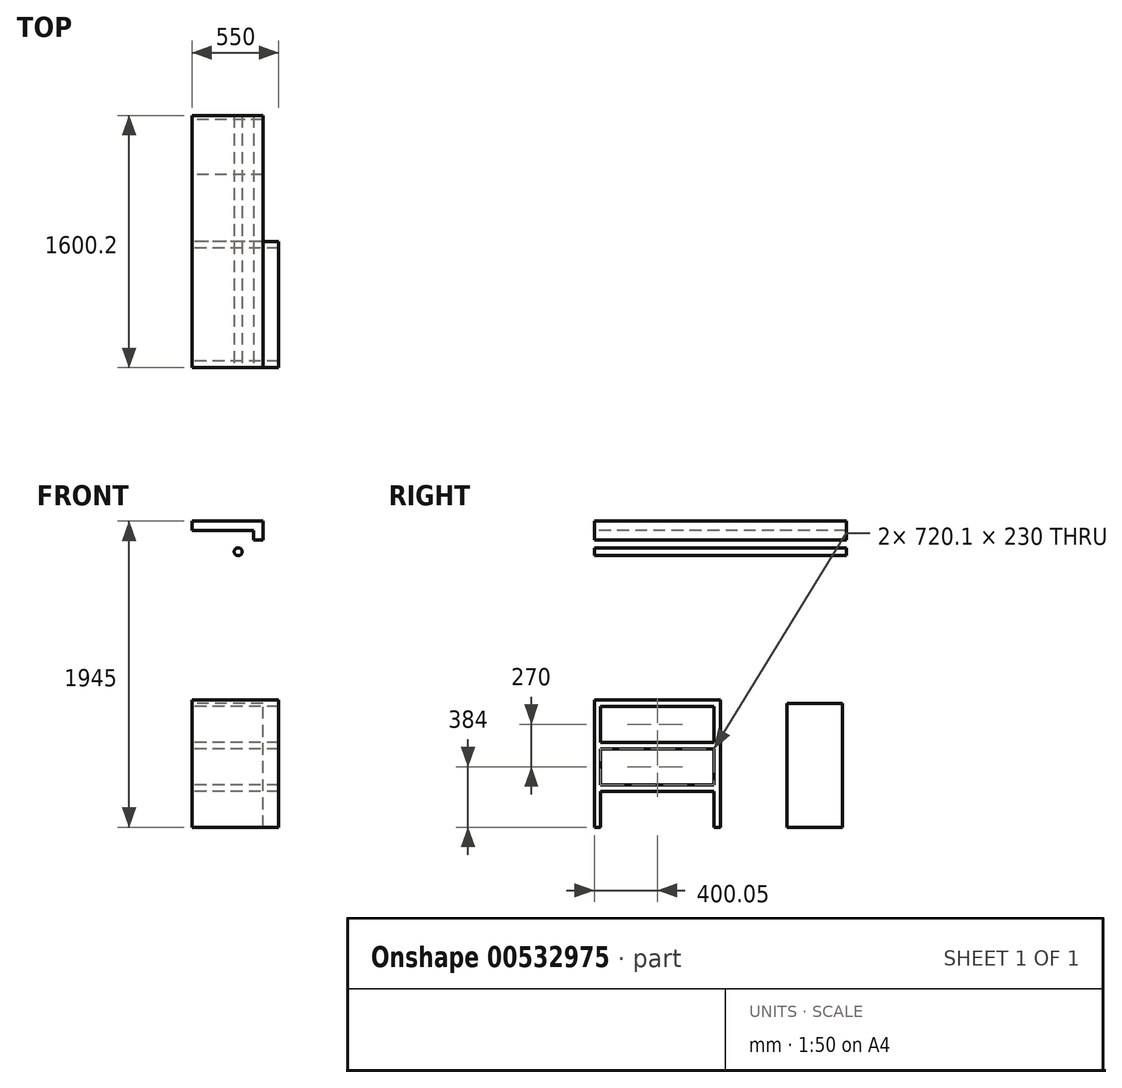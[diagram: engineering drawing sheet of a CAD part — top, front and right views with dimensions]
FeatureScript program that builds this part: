
annotation { "Feature Type Name" : "Feature", "Feature Type Description" : "" }
export const myFeature = defineFeature(function(context is Context, id is Id, definition is map)
    precondition{}
    {
        {
            var Q0;
            Q0=qCreatedBy(makeId("Front.planeOp"),FACE);
            var sketch = newSketch(context, id + "F0", { "sketchPlane" : qUnion([Q0])});
            skLineSegment(sketch, "E0.bottom", {"start": v(0, 0) * mm, "end": v(584.2, 0) * mm});
            skLineSegment(sketch, "E0.top", {"start": v(0, 2311.4) * mm, "end": v(584.2, 2311.4) * mm});
            skLineSegment(sketch, "E0.left", {"start": v(0, 0) * mm, "end": v(0, 2311.4) * mm});
            skLineSegment(sketch, "E0.right", {"start": v(584.2, 0) * mm, "end": v(584.2, 2311.4) * mm});
            skSolve(sketch);
        }
        {
            var Q0;
            Q0=qCreatedBy(makeId("Right.planeOp"),FACE);
            var sketch = newSketch(context, id + "F1", { "sketchPlane" : qUnion([Q0])});
            skLineSegment(sketch, "E1.bottom", {"start": v(0, 0) * mm, "end": v(1600.2, 0) * mm});
            skLineSegment(sketch, "E1.top", {"start": v(0, 2311.4) * mm, "end": v(1600.2, 2311.4) * mm});
            skLineSegment(sketch, "E1.left", {"start": v(0, 0) * mm, "end": v(0, 2311.4) * mm});
            skLineSegment(sketch, "E1.right", {"start": v(1600.2, 0) * mm, "end": v(1600.2, 2311.4) * mm});
            skSolve(sketch);
        }
        {
            var Q0;
            Q0=qCreatedBy(makeId("Front.planeOp"),FACE);
            var Q1;
            Q1=sQuery(id+"F1.wireOp",VERTEX,"E1.right.start");
            cPlane(context, id + "F2", {"entities" : qUnion([Q0, Q1]), "cplaneType" : CPlaneType.PLANE_POINT, "offset" : 25 * mm, "width" : 150 * mm, "height" : 150 * mm});
        }
        {
            var Q0;
            Q0=sQuery(id+"F0.wireOp",VERTEX,"E0.right.end");
            var Q1;
            Q1=sQuery(id+"F1.wireOp",VERTEX,"E1.left.end");
            var Q2;
            Q2=sQuery(id+"F1.wireOp",VERTEX,"E1.right.end");
            cPlane(context, id + "F3", {"entities" : qUnion([Q0, Q1, Q2]), "cplaneType" : CPlaneType.THREE_POINT, "offset" : 25 * mm, "width" : 150 * mm, "height" : 150 * mm});
        }
        {
            var Q0;
            Q0=qCreatedBy(id+"F2.planeOp",FACE);
            var sketch = newSketch(context, id + "F4", { "sketchPlane" : qUnion([Q0])});
            skLineSegment(sketch, "E2.bottom", {"start": v(0, 0) * mm, "end": v(584.2, 0) * mm});
            skLineSegment(sketch, "E2.top", {"start": v(0, 2311.4) * mm, "end": v(584.2, 2311.4) * mm});
            skLineSegment(sketch, "E2.left", {"start": v(0, 0) * mm, "end": v(0, 2311.4) * mm});
            skLineSegment(sketch, "E2.right", {"start": v(584.2, 0) * mm, "end": v(584.2, 2311.4) * mm});
            skSolve(sketch);
        }
        {
            var Q0;
            Q0=qCreatedBy(id+"F3.planeOp",FACE);
            var sketch = newSketch(context, id + "F5", { "sketchPlane" : qUnion([Q0])});
            skLineSegment(sketch, "E3.bottom", {"start": v(0, 0) * mm, "end": v(584.2, 0) * mm});
            skLineSegment(sketch, "E3.top", {"start": v(0, 1600.2) * mm, "end": v(584.2, 1600.2) * mm});
            skLineSegment(sketch, "E3.left", {"start": v(0, 0) * mm, "end": v(0, 1600.2) * mm});
            skLineSegment(sketch, "E3.right", {"start": v(584.2, 0) * mm, "end": v(584.2, 1600.2) * mm});
            skSolve(sketch);
        }
        {
            var Q0;
            Q0=qCreatedBy(makeId("Front.planeOp"),FACE);
            var sketch = newSketch(context, id + "F6", { "sketchPlane" : qUnion([Q0])});
            skCircle(sketch, "E4", {"center": v(292.1, 1750) * mm, "radius": 25 * mm});
            skLineSegment(sketch, "E5", {"start": v(292.1, 2311.4) * mm, "end": v(292.1, 0) * mm, "construction": true});
            skLineSegment(sketch, "E6.bottom", {"start": v(0, 1945) * mm, "end": v(450, 1945) * mm});
            skLineSegment(sketch, "E6.top", {"start": v(390, 1825) * mm, "end": v(450, 1825) * mm});
            skLineSegment(sketch, "E6.left", {"start": v(0, 1945) * mm, "end": v(0, 1885) * mm});
            skLineSegment(sketch, "E6.right", {"start": v(450, 1945) * mm, "end": v(450, 1825) * mm});
            skLineSegment(sketch, "E7.bottom", {"start": v(0, 1885) * mm, "end": v(390, 1885) * mm});
            skLineSegment(sketch, "E7.right", {"start": v(390, 1885) * mm, "end": v(390, 1825) * mm});
            skSolve(sketch);
        }
        {
            var Q0;
            Q0 = qSketchRegion(id + "F6", true);
            var Q1;
            Q1=qCreatedBy(id+"F2.planeOp",FACE);
            extrude(context, id + "F7", {"entities" : qUnion([Q0]), "endBound" : BoundingType.UP_TO_SURFACE, "oppositeDirection" : true, "depth" : 25 * mm, "endBoundEntityFace" : qUnion([Q1]), "offsetDistance" : 25 * mm});
        }
        {
            var Q0;
            Q0=qCreatedBy(makeId("Right.planeOp"),FACE);
            var sketch = newSketch(context, id + "F8", { "sketchPlane" : qUnion([Q0])});
            skLineSegment(sketch, "E8.bottom", {"start": v(0, 809) * mm, "end": v(800.1, 809) * mm});
            skLineSegment(sketch, "E8.top", {"start": v(40, 769) * mm, "end": v(760.1, 769) * mm});
            skLineSegment(sketch, "E8.left", {"start": v(0, 809) * mm, "end": v(0, 0) * mm});
            skLineSegment(sketch, "E9.top", {"start": v(800.1, 0) * mm, "end": v(760.1, 0) * mm});
            skLineSegment(sketch, "E9.right", {"start": v(760.1, 769) * mm, "end": v(760.1, 539) * mm});
            skLineSegment(sketch, "E10", {"start": v(800.1, 809) * mm, "end": v(800.1, 0) * mm});
            skLineSegment(sketch, "E11.bottom", {"start": v(760.1, 539) * mm, "end": v(40, 539) * mm});
            skLineSegment(sketch, "E11.top", {"start": v(760.1, 499) * mm, "end": v(40, 499) * mm});
            skLineSegment(sketch, "E12.bottom", {"start": v(0, 0) * mm, "end": v(40, 0) * mm});
            skLineSegment(sketch, "E13.trimOffspring", {"start": v(40, 539) * mm, "end": v(40, 769) * mm});
            skLineSegment(sketch, "E14.bottom", {"start": v(40, 499) * mm, "end": v(760.1, 499) * mm});
            skLineSegment(sketch, "E14.top", {"start": v(40, 269) * mm, "end": v(760.1, 269) * mm});
            skLineSegment(sketch, "E14.left", {"start": v(40, 499) * mm, "end": v(40, 269) * mm});
            skLineSegment(sketch, "E14.right", {"start": v(760.1, 499) * mm, "end": v(760.1, 269) * mm});
            skLineSegment(sketch, "E15.top", {"start": v(40, 229) * mm, "end": v(760.1, 229) * mm});
            skLineSegment(sketch, "E15.left", {"start": v(40, 0) * mm, "end": v(40, 229) * mm});
            skLineSegment(sketch, "E15.right", {"start": v(760.1, 0) * mm, "end": v(760.1, 229) * mm});
            skSolve(sketch);
        }
        {
            var Q0;
            Q0 = qSketchRegion(id + "F8", true);
            extrude(context, id + "F9", {"entities" : qUnion([Q0]), "depth" : 550 * mm, "offsetDistance" : 25 * mm});
        }
        {
            var Q0;
            Q0 = qSketchRegion(id + "F8", true);
            extrude(context, id + "F10", {"entities" : qUnion([Q0]), "operationType" : NewBodyOperationType.ADD, "depth" : 25 * mm, "offsetDistance" : 25 * mm});
        }
        {
            var Q0;
            Q0=qCreatedBy(makeId("Right.planeOp"),FACE);
            var sketch = newSketch(context, id + "F11", { "sketchPlane" : qUnion([Q0])});
            skLineSegment(sketch, "E16.bottom", {"start": v(1225.2, 0) * mm, "end": v(1575.2, 0) * mm});
            skLineSegment(sketch, "E16.top", {"start": v(1225.2, 787.4) * mm, "end": v(1575.2, 787.4) * mm});
            skLineSegment(sketch, "E16.left", {"start": v(1225.2, 0) * mm, "end": v(1225.2, 787.4) * mm});
            skLineSegment(sketch, "E16.right", {"start": v(1575.2, 0) * mm, "end": v(1575.2, 787.4) * mm});
            skSolve(sketch);
        }
        {
            var Q0;
            Q0 = qSketchRegion(id + "F11", true);
            extrude(context, id + "F12", {"entities" : qUnion([Q0]), "depth" : 450 * mm, "offsetDistance" : 25 * mm});
        }
    });
